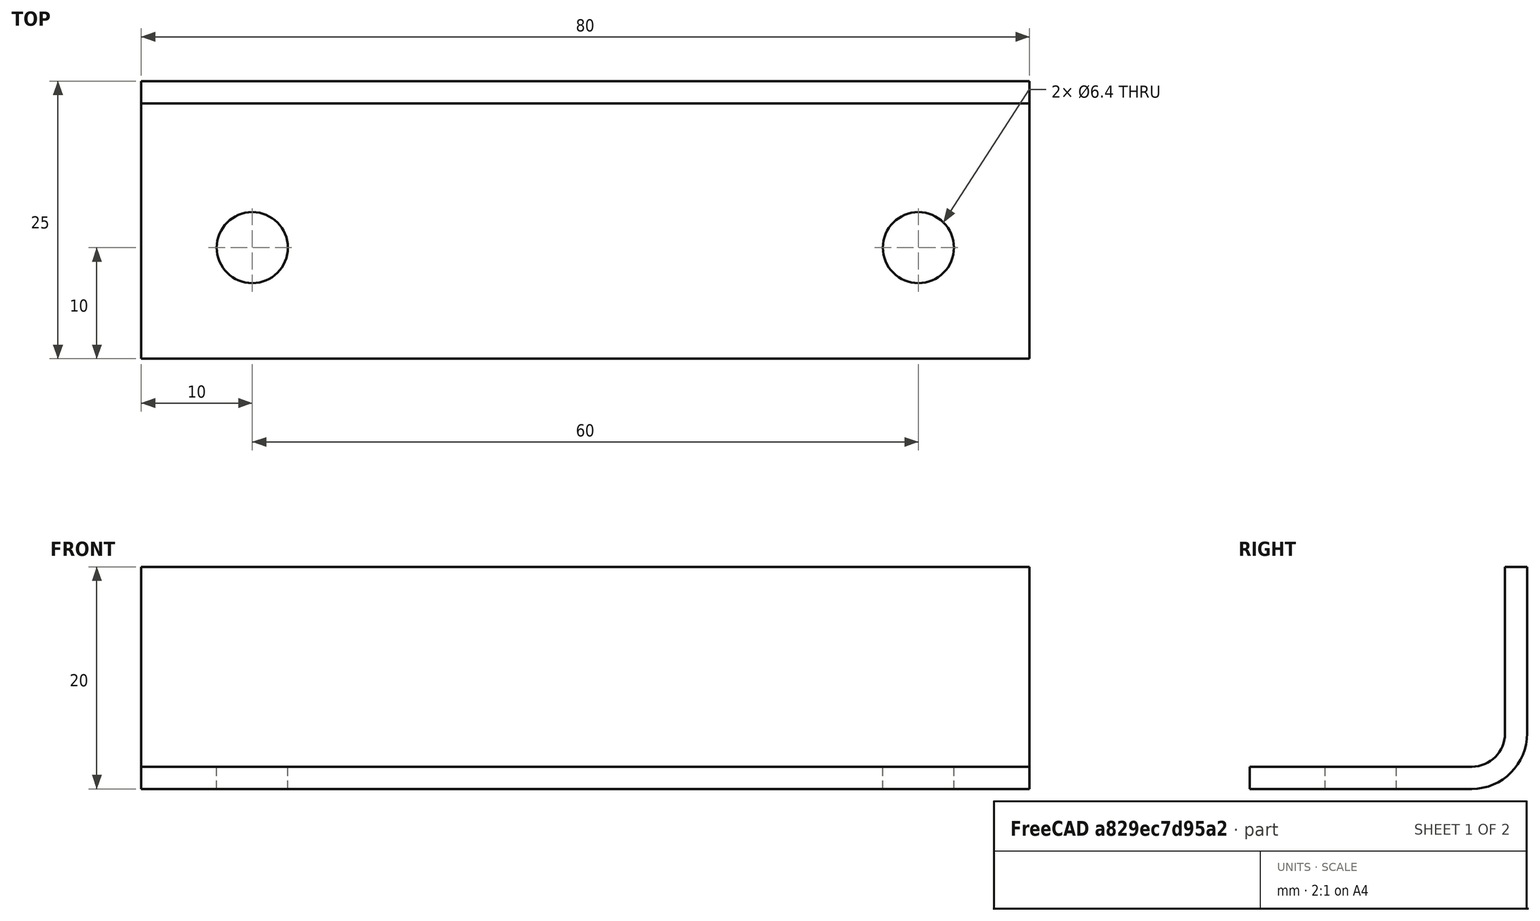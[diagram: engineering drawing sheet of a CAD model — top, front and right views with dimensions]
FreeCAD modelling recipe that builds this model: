
FCSTD DOCUMENT  (FreeCAD 1.0R39319 (Git))
Label: OCT-CHBRA-AB
License: Creative Commons Attribution 4.0
LicenseURL: https://creativecommons.org/licenses/by/4.0/
objects: TechDraw::DrawViewDimension×9, TechDraw::DrawProjGroupItem×2, PartDesign::FeaturePython×1, Sketcher::SketchObject×1, PartDesign::Hole×1, PartDesign::Body×1, TechDraw::DrawSVGTemplate×1, TechDraw::DrawProjGroup×1, TechDraw::DrawPage×1
note: 22 computed .brp shape members not serialized (recipe doc carries the construction recipe); baked Part::Feature solids carry a one-line shape summary decoded from their .brp

FEATURE [PartDesign::FeaturePython] BaseShape  # WARN: FeaturePython — macro-defined, semantics opaque (R4)
  Suppressed = false
  fillGaps = true
  flangeWidth = 5
  height = 20
  length = 80
  originLoc = 5
  radius = 3
  shapeType = 1
  thickness = 2
  width = 25
FEATURE [Sketcher::SketchObject] Sketch
  ArcFitTolerance = 1e-06
  AttachmentSupport = -> [XY_Plane001]
  FullyConstrained = true
  MakeInternals = false
  MapMode = 5
  sketch-geometry (2):
    g0: Circle CenterX=-30 CenterY=-15 CenterZ=0 NormalX=0 NormalY=0 NormalZ=1 AngleXU=0 Radius=2.5
    g1: Circle CenterX=30 CenterY=-15 CenterZ=0 NormalX=0 NormalY=0 NormalZ=1 AngleXU=0 Radius=2.5
  constraints (5):
    c: Symmetric(g0,g1,g-2)
    c: Equal(g0,g1)
    c: Diameter(g0) = 5
    c: Distance(g0,g-1) = 15
    c: DistanceX(g0,g1) = 60
FEATURE [PartDesign::Hole] Hole
  BaseFeature = -> BaseShape
  CustomThreadClearance = 0
  Depth = 25
  DepthType = 0
  Diameter = 6.4
  DrillForDepth = false
  DrillPoint = 1
  DrillPointAngle = 118
  HoleCutCountersinkAngle = 90
  HoleCutCustomValues = false
  HoleCutDepth = 0
  HoleCutDiameter = 0
  HoleCutType = 0
  ModelThread = false
  Profile = -> Sketch
  Reversed = true
  Suppressed = false
  Tapered = false
  TaperedAngle = 90
  ThreadClass = 0
  ThreadDepth = 25
  ThreadDepthType = 0
  ThreadDirection = 0
  ThreadFit = 1
  ThreadSize = 14
  ThreadType = 1
  Threaded = false
  UseCustomThreadClearance = false
FEATURE [PartDesign::Body] Body001  label="OCT-CHBRA-AB"
  AllowCompound = false
  Group = -> [BaseShape,Sketch,Hole]
  Origin = -> Origin001
  Tip = -> Hole
FEATURE [TechDraw::DrawSVGTemplate] Template
  EditableTexts = approval_person=S. Aphelion; creator=Michael Stoll; date_of_issue=14/02/2026; document_status=In preparation; document_type=Component Drawing; drawing_number=DN; general_tolerances=ISO 2768-m; language_code=EN; part_material=Mild Steel; responsible_department=RD; revision_index=A; scale=1 : 1; sheet_number=1 / 1; supplementary_title_1=Chamber Brace; title=OCT-CHBRA-AB
  Height = 297
  Orientation = 1
  Template = C:/Program Files/FreeCAD 1.0/data/Mod/TechDraw/Templates/A3_Landscape_ISO5457_advanced.svg
  Width = 420
FEATURE [TechDraw::DrawProjGroupItem] View  label="Front"
  CoarseView = false
  Direction = (0,0,1)
  Focus = 100
  HardHidden = false
  IsoCount = 0
  IsoHidden = false
  IsoVisible = false
  LockPosition = true
  Perspective = false
  Rotation = 0
  RotationVector = (1,0,0)
  ScaleType = 2
  ScrubCount = 1
  SeamHidden = false
  SeamVisible = false
  SmoothHidden = false
  SmoothVisible = true
  Source = -> [Body001]
  Type = 0
  X = 0
  XDirection = (1,0,0)
  Y = 0
FEATURE [TechDraw::DrawProjGroupItem] ProjItem  label="Right"
  CoarseView = false
  Direction = (1,0,1e-16)
  Focus = 100
  HardHidden = false
  IsoCount = 0
  IsoHidden = false
  IsoVisible = false
  LockPosition = false
  Perspective = false
  Rotation = 0
  RotationVector = (1,0,0)
  ScaleType = 0
  ScrubCount = 1
  SeamHidden = false
  SeamVisible = false
  SmoothHidden = false
  SmoothVisible = true
  Source = -> [Body001]
  Type = 2
  X = 100
  XDirection = (1e-16,0,-1)
  Y = 0
FEATURE [TechDraw::DrawProjGroup] ProjGroup
  Anchor = -> View
  AutoDistribute = true
  LockPosition = false
  ProjectionType = 1
  Rotation = 0
  ScaleType = 0
  Source = -> [Body001]
  Views = -> [View,ProjItem]
  X = 171.603
  Y = 151.276
  spacingX = 50
  spacingY = 15
FEATURE [TechDraw::DrawViewDimension] Dimension
  AngleOverride = false
  Arbitrary = false
  ArbitraryTolerances = false
  BoxCorners = (2) [(-40,-12.5,-1e-07),(40,12.5,1e-07)]
  EqualTolerance = true
  ExtensionAngle = 0
  FormatSpec = %.1f
  FormatSpecOverTolerance = %+.1f
  FormatSpecUnderTolerance = %+.1f
  Inverted = false
  LineAngle = 0
  LockPosition = false
  MeasureType = 1
  OverTolerance = 0
  References2D = -> [View]
  Rotation = 0
  ScaleType = 0
  TheoreticalExact = false
  Type = 1
  UnderTolerance = 0
  X = 0
  Y = 37.5718
FEATURE [TechDraw::DrawViewDimension] Dimension001
  AngleOverride = false
  Arbitrary = false
  ArbitraryTolerances = false
  BoxCorners = (2) [(-10,-12.5,0),(10,12.5,0)]
  EqualTolerance = true
  ExtensionAngle = 0
  FormatSpec = %.1f
  FormatSpecOverTolerance = %+.1f
  FormatSpecUnderTolerance = %+.1f
  Inverted = false
  LineAngle = 0
  LockPosition = false
  MeasureType = 1
  OverTolerance = 0
  References2D = -> [ProjItem]
  Rotation = 0
  ScaleType = 0
  TheoreticalExact = false
  Type = 2
  UnderTolerance = 0
  X = 28.0977
  Y = 0
FEATURE [TechDraw::DrawViewDimension] Dimension002
  AngleOverride = false
  Arbitrary = false
  ArbitraryTolerances = false
  BoxCorners = (2) [(-10,-12.5,0),(10,12.5,0)]
  EqualTolerance = true
  ExtensionAngle = 0
  FormatSpec = %.1f
  FormatSpecOverTolerance = %+.1f
  FormatSpecUnderTolerance = %+.1f
  Inverted = false
  LineAngle = 0
  LockPosition = false
  MeasureType = 1
  OverTolerance = 0
  References2D = -> [ProjItem]
  Rotation = 0
  ScaleType = 0
  TheoreticalExact = false
  Type = 1
  UnderTolerance = 0
  X = 0
  Y = 31.0972
FEATURE [TechDraw::DrawViewDimension] Dimension003
  AngleOverride = false
  Arbitrary = false
  ArbitraryTolerances = false
  BoxCorners = (2) [(-10,-12.5,0),(10,12.5,0)]
  EqualTolerance = true
  ExtensionAngle = 0
  FormatSpec = %.1f
  FormatSpecOverTolerance = %+.1f
  FormatSpecUnderTolerance = %+.1f
  Inverted = false
  LineAngle = 0
  LockPosition = false
  MeasureType = 1
  OverTolerance = 0
  References2D = -> [ProjItem]
  Rotation = 0
  ScaleType = 0
  TheoreticalExact = false
  Type = 2
  UnderTolerance = 0
  X = -25.5968
  Y = 11.5
FEATURE [TechDraw::DrawViewDimension] Dimension004
  AngleOverride = false
  Arbitrary = false
  ArbitraryTolerances = false
  BoxCorners = (2) [(-10,-12.5,0),(10,12.5,0)]
  EqualTolerance = true
  ExtensionAngle = 0
  FormatSpec = R%.1f
  FormatSpecOverTolerance = %+.1f
  FormatSpecUnderTolerance = %+.1f
  Inverted = false
  LineAngle = 0
  LockPosition = false
  MeasureType = 1
  OverTolerance = 0
  References2D = -> [ProjItem]
  Rotation = 0
  ScaleType = 0
  TheoreticalExact = false
  Type = 4
  UnderTolerance = 0
  X = -22.9376
  Y = -2.14254
FEATURE [TechDraw::DrawViewDimension] Dimension005
  AngleOverride = false
  Arbitrary = false
  ArbitraryTolerances = false
  BoxCorners = (2) [(-40,-12.5,-1e-07),(40,12.5,1e-07)]
  EqualTolerance = true
  ExtensionAngle = 0
  FormatSpec = %.1f
  FormatSpecOverTolerance = %+.1f
  FormatSpecUnderTolerance = %+.1f
  Inverted = false
  LineAngle = 0
  LockPosition = false
  MeasureType = 1
  OverTolerance = 0
  References2D = -> [View]
  Rotation = 0
  ScaleType = 0
  TheoreticalExact = false
  Type = 0
  UnderTolerance = 0
  X = -59.2267
  Y = -7.5
FEATURE [TechDraw::DrawViewDimension] Dimension006
  AngleOverride = false
  Arbitrary = false
  ArbitraryTolerances = false
  BoxCorners = (2) [(-40,-12.5,-1e-07),(40,12.5,1e-07)]
  EqualTolerance = true
  ExtensionAngle = 0
  FormatSpec = %.1f
  FormatSpecOverTolerance = %+.1f
  FormatSpecUnderTolerance = %+.1f
  Inverted = false
  LineAngle = 0
  LockPosition = false
  MeasureType = 1
  OverTolerance = 0
  References2D = -> [View]
  Rotation = 0
  ScaleType = 0
  TheoreticalExact = false
  Type = 0
  UnderTolerance = 0
  X = -47.1685
  Y = -29.9473
FEATURE [TechDraw::DrawViewDimension] Dimension007
  AngleOverride = false
  Arbitrary = false
  ArbitraryTolerances = false
  BoxCorners = (2) [(-40,-12.5,-1e-07),(40,12.5,1e-07)]
  EqualTolerance = true
  ExtensionAngle = 0
  FormatSpec = %.1f
  FormatSpecOverTolerance = %+.1f
  FormatSpecUnderTolerance = %+.1f
  Inverted = false
  LineAngle = 0
  LockPosition = false
  MeasureType = 1
  OverTolerance = 0
  References2D = -> [View]
  Rotation = 0
  ScaleType = 0
  TheoreticalExact = false
  Type = 1
  UnderTolerance = 0
  X = 0
  Y = -29.9473
FEATURE [TechDraw::DrawViewDimension] Dimension008
  AngleOverride = false
  Arbitrary = false
  ArbitraryTolerances = false
  BoxCorners = (2) [(-40,-12.5,-1e-07),(40,12.5,1e-07)]
  EqualTolerance = true
  ExtensionAngle = 0
  FormatSpec = ⌀%.1f
  FormatSpecOverTolerance = %+.1f
  FormatSpecUnderTolerance = %+.1f
  Inverted = false
  LineAngle = 0
  LockPosition = false
  MeasureType = 1
  OverTolerance = 0
  References2D = -> [View]
  Rotation = 0
  ScaleType = 0
  TheoreticalExact = false
  Type = 5
  UnderTolerance = 0
  X = 62.4995
  Y = -20.8805
FEATURE [TechDraw::DrawPage] Page
  KeepUpdated = true
  NextBalloonIndex = 1
  ProjectionType = 1
  Template = -> Template
  Views = -> [ProjGroup,Dimension,Dimension001,Dimension002,Dimension003,Dimension004,Dimension005,Dimension006,Dimension007,Dimension008]
